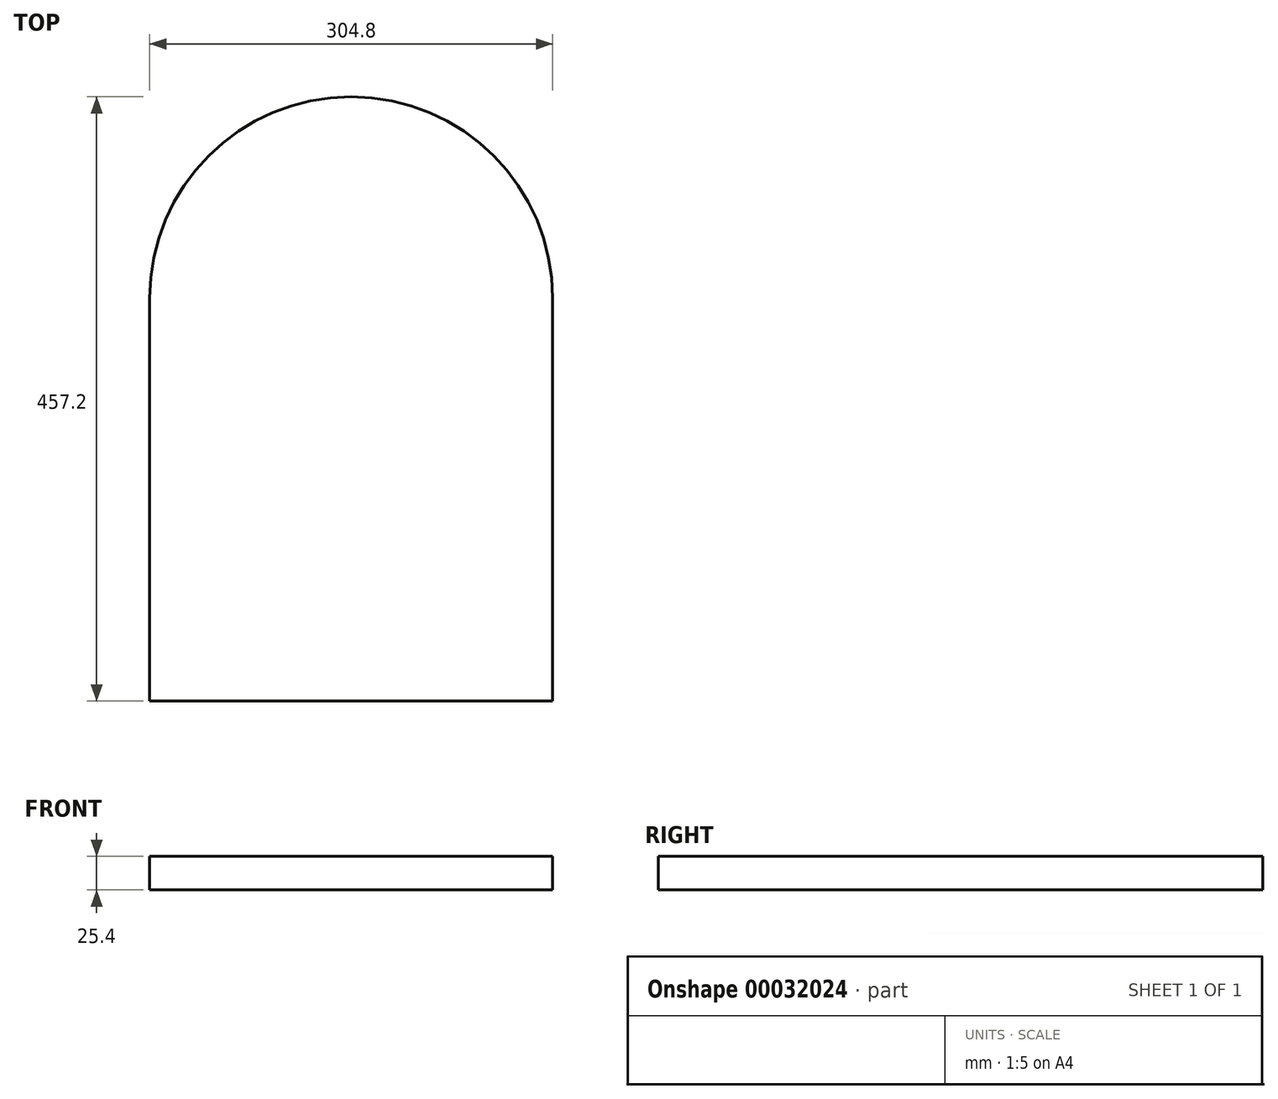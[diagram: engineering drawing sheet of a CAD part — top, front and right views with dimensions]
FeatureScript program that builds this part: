
annotation { "Feature Type Name" : "Feature", "Feature Type Description" : "" }
export const myFeature = defineFeature(function(context is Context, id is Id, definition is map)
    precondition{}
    {
        {
            var Q0;
            Q0=qCreatedBy(makeId("Top.planeOp"),FACE);
            var sketch = newSketch(context, id + "F0", { "sketchPlane" : qUnion([Q0])});
            skLineSegment(sketch, "E0.bottom", {"start": v(0, 0) * mm, "end": v(304.8, 0) * mm});
            skLineSegment(sketch, "E0.left", {"start": v(0, 0) * mm, "end": v(0, 304.8) * mm});
            skLineSegment(sketch, "E0.right", {"start": v(304.8, 0) * mm, "end": v(304.8, 304.8) * mm});
            skArc(sketch, "E1", {"start": v(304.8, 304.8) * mm, "mid": v(152.4, 457.2) * mm, "end": v(0, 304.8) * mm});
            skSolve(sketch);
        }
        {
            var Q0;
            Q0=makeQuery(id+"F0.imprint","IMPRINT",FACE,{"disambiguationData":[TD([[makeQuery(id+"F0.imprint","IMPRINT",EDGE,{"derivedFrom":sQuery(id+"F0.wireOp",EDGE,"E0.bottom")}),1.0]])]});
            extrude(context, id + "F1", {"entities" : qUnion([Q0]), "depth" : 25.4 * mm});
        }
    });
